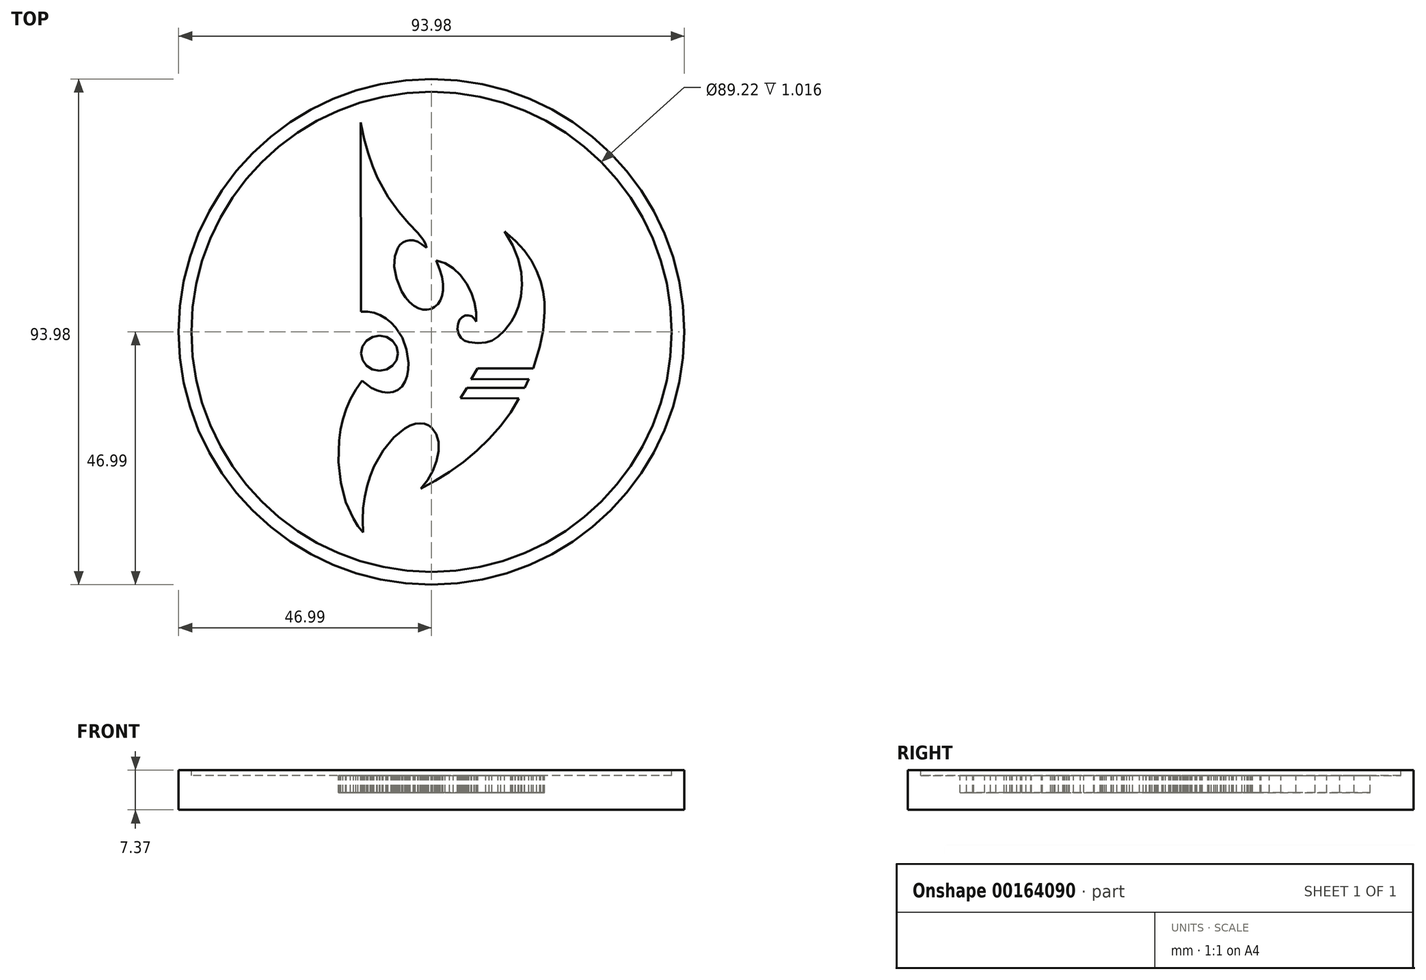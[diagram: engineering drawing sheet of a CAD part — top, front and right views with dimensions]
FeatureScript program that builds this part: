
annotation { "Feature Type Name" : "Feature", "Feature Type Description" : "" }
export const myFeature = defineFeature(function(context is Context, id is Id, definition is map)
    precondition{}
    {
        {
            var Q0;
            Q0=qCreatedBy(makeId("Front.planeOp"),FACE);
            var sketch = newSketch(context, id + "F0", { "sketchPlane" : qUnion([Q0])});
            skLineSegment(sketch, "E0", {"start": v(-47, 7.37) * mm, "end": v(-44.6, 7.37) * mm});
            skLineSegment(sketch, "E1", {"start": v(-44.6, 7.37) * mm, "end": v(-44.6, 6.35) * mm});
            skLineSegment(sketch, "E2", {"start": v(-44.6, 6.35) * mm, "end": v(0, 6.35) * mm});
            skLineSegment(sketch, "E3", {"start": v(0, 6.35) * mm, "end": v(0, 0) * mm});
            skLineSegment(sketch, "E4", {"start": v(0, 0) * mm, "end": v(-47, 0) * mm});
            skLineSegment(sketch, "E5", {"start": v(-47, 0) * mm, "end": v(-47, 7.37) * mm});
            skSolve(sketch);
        }
        {
            var Q0;
            Q0=makeQuery(id+"F0.imprint","IMPRINT",FACE,{"disambiguationData":[TD([[makeQuery(id+"F0.imprint","IMPRINT",EDGE,{"derivedFrom":sQuery(id+"F0.wireOp",EDGE,"E0")}),-1.0]])]});
            var Q1;
            Q1=sQuery(id+"F0.wireOp",EDGE,"E3");
            revolve(context, id + "F1", {"entities" : qUnion([Q0]), "axis" : qUnion([Q1]), "revolveType" : RevolveType.FULL});
        }
        {
            var Q0;
            Q0=makeQuery(id+"F1.opRevolve","SWEPT_FACE",FACE,{"disambiguationData":[OSD([sQuery(id+"F0.wireOp",EDGE,"E2")])]});
            var sketch = newSketch(context, id + "F2", { "sketchPlane" : qUnion([Q0])});
            skLineSegment(sketch, "E6", {"start": v(-13.1, 3.76) * mm, "end": v(-13.14, 38.91) * mm});
            skLineSegment(sketch, "E7", {"start": v(-13.14, 38.91) * mm, "end": v(-12.53, 35.9) * mm});
            skLineSegment(sketch, "E8", {"start": v(-12.53, 35.9) * mm, "end": v(-11.8, 33.21) * mm});
            skLineSegment(sketch, "E9", {"start": v(-11.8, 33.21) * mm, "end": v(-10.96, 30.8) * mm});
            skLineSegment(sketch, "E10", {"start": v(-10.96, 30.8) * mm, "end": v(-10.06, 28.67) * mm});
            skLineSegment(sketch, "E11", {"start": v(-10.06, 28.67) * mm, "end": v(-8.1, 25.1) * mm});
            skLineSegment(sketch, "E12", {"start": v(-8.1, 25.1) * mm, "end": v(-6.08, 22.32) * mm});
            skLineSegment(sketch, "E13", {"start": v(-6.08, 22.32) * mm, "end": v(-4.18, 20.16) * mm});
            skLineSegment(sketch, "E14", {"start": v(-4.18, 20.16) * mm, "end": v(-2.58, 18.44) * mm});
            skLineSegment(sketch, "E15", {"start": v(-2.58, 18.44) * mm, "end": v(-1.44, 16.97) * mm});
            skLineSegment(sketch, "E16", {"start": v(-1.44, 16.97) * mm, "end": v(-1.1, 16.29) * mm});
            skLineSegment(sketch, "E17", {"start": v(-1.1, 16.29) * mm, "end": v(-0.93, 15.6) * mm});
            skLineSegment(sketch, "E18", {"start": v(-0.93, 15.6) * mm, "end": v(-1.78, 16.28) * mm});
            skLineSegment(sketch, "E19", {"start": v(-1.78, 16.28) * mm, "end": v(-2.59, 16.74) * mm});
            skLineSegment(sketch, "E20", {"start": v(-2.59, 16.74) * mm, "end": v(-3.35, 16.99) * mm});
            skLineSegment(sketch, "E21", {"start": v(-3.35, 16.99) * mm, "end": v(-4.07, 17.04) * mm});
            skLineSegment(sketch, "E22", {"start": v(-4.07, 17.04) * mm, "end": v(-4.73, 16.92) * mm});
            skLineSegment(sketch, "E23", {"start": v(-4.73, 16.92) * mm, "end": v(-5.32, 16.62) * mm});
            skLineSegment(sketch, "E24", {"start": v(-5.32, 16.62) * mm, "end": v(-5.83, 16.18) * mm});
            skLineSegment(sketch, "E25", {"start": v(-5.83, 16.18) * mm, "end": v(-6.26, 15.6) * mm});
            skLineSegment(sketch, "E26", {"start": v(-6.26, 15.6) * mm, "end": v(-6.82, 14.05) * mm});
            skLineSegment(sketch, "E27", {"start": v(-6.82, 14.05) * mm, "end": v(-6.93, 12.12) * mm});
            skLineSegment(sketch, "E28", {"start": v(-6.93, 12.12) * mm, "end": v(-6.52, 9.9) * mm});
            skLineSegment(sketch, "E29", {"start": v(-6.52, 9.9) * mm, "end": v(-5.53, 7.5) * mm});
            skLineSegment(sketch, "E30", {"start": v(-5.53, 7.5) * mm, "end": v(-4.83, 6.4) * mm});
            skLineSegment(sketch, "E31", {"start": v(-4.83, 6.4) * mm, "end": v(-4.07, 5.5) * mm});
            skLineSegment(sketch, "E32", {"start": v(-4.07, 5.5) * mm, "end": v(-3.27, 4.85) * mm});
            skLineSegment(sketch, "E33", {"start": v(-3.27, 4.85) * mm, "end": v(-2.45, 4.4) * mm});
            skLineSegment(sketch, "E34", {"start": v(-2.45, 4.4) * mm, "end": v(-1.63, 4.16) * mm});
            skLineSegment(sketch, "E35", {"start": v(-1.63, 4.16) * mm, "end": v(-0.84, 4.12) * mm});
            skLineSegment(sketch, "E36", {"start": v(-0.84, 4.12) * mm, "end": v(-0.1, 4.27) * mm});
            skLineSegment(sketch, "E37", {"start": v(-0.1, 4.27) * mm, "end": v(0.58, 4.61) * mm});
            skLineSegment(sketch, "E38", {"start": v(0.58, 4.61) * mm, "end": v(1.16, 5.13) * mm});
            skLineSegment(sketch, "E39", {"start": v(1.16, 5.13) * mm, "end": v(1.63, 5.83) * mm});
            skLineSegment(sketch, "E40", {"start": v(1.63, 5.83) * mm, "end": v(1.97, 6.69) * mm});
            skLineSegment(sketch, "E41", {"start": v(1.97, 6.69) * mm, "end": v(2.15, 7.7) * mm});
            skLineSegment(sketch, "E42", {"start": v(2.15, 7.7) * mm, "end": v(2.14, 8.88) * mm});
            skLineSegment(sketch, "E43", {"start": v(2.14, 8.88) * mm, "end": v(1.94, 10.2) * mm});
            skLineSegment(sketch, "E44", {"start": v(1.94, 10.2) * mm, "end": v(1.52, 11.65) * mm});
            skLineSegment(sketch, "E45", {"start": v(1.52, 11.65) * mm, "end": v(0.85, 13.24) * mm});
            skLineSegment(sketch, "E46", {"start": v(0.85, 13.24) * mm, "end": v(2.52, 12.74) * mm});
            skLineSegment(sketch, "E47", {"start": v(2.52, 12.74) * mm, "end": v(4.04, 11.8) * mm});
            skLineSegment(sketch, "E48", {"start": v(4.04, 11.8) * mm, "end": v(5.37, 10.52) * mm});
            skLineSegment(sketch, "E49", {"start": v(5.37, 10.52) * mm, "end": v(6.5, 8.97) * mm});
            skLineSegment(sketch, "E50", {"start": v(6.5, 8.97) * mm, "end": v(7.39, 7.25) * mm});
            skLineSegment(sketch, "E51", {"start": v(7.39, 7.25) * mm, "end": v(8, 5.43) * mm});
            skLineSegment(sketch, "E52", {"start": v(8, 5.43) * mm, "end": v(8.32, 3.62) * mm});
            skLineSegment(sketch, "E53", {"start": v(8.32, 3.62) * mm, "end": v(8.3, 1.88) * mm});
            skLineSegment(sketch, "E54", {"start": v(8.3, 1.88) * mm, "end": v(7.95, 2.5) * mm});
            skLineSegment(sketch, "E55", {"start": v(7.95, 2.5) * mm, "end": v(7.44, 2.9) * mm});
            skLineSegment(sketch, "E56", {"start": v(7.44, 2.9) * mm, "end": v(6.85, 3.07) * mm});
            skLineSegment(sketch, "E57", {"start": v(6.85, 3.07) * mm, "end": v(6.24, 3.02) * mm});
            skLineSegment(sketch, "E58", {"start": v(6.24, 3.02) * mm, "end": v(5.67, 2.74) * mm});
            skLineSegment(sketch, "E59", {"start": v(5.67, 2.74) * mm, "end": v(5.2, 2.22) * mm});
            skLineSegment(sketch, "E60", {"start": v(5.2, 2.22) * mm, "end": v(4.9, 1.48) * mm});
            skLineSegment(sketch, "E61", {"start": v(4.9, 1.48) * mm, "end": v(4.83, 0.5) * mm});
            skLineSegment(sketch, "E62", {"start": v(4.83, 0.5) * mm, "end": v(5.04, -0.46) * mm});
            skLineSegment(sketch, "E63", {"start": v(5.04, -0.46) * mm, "end": v(5.5, -1.16) * mm});
            skLineSegment(sketch, "E64", {"start": v(5.5, -1.16) * mm, "end": v(6.16, -1.64) * mm});
            skLineSegment(sketch, "E65", {"start": v(6.16, -1.64) * mm, "end": v(6.94, -1.93) * mm});
            skLineSegment(sketch, "E66", {"start": v(6.94, -1.93) * mm, "end": v(8.64, -2.1) * mm});
            skLineSegment(sketch, "E67", {"start": v(8.64, -2.1) * mm, "end": v(10.09, -1.98) * mm});
            skLineSegment(sketch, "E68", {"start": v(10.09, -1.98) * mm, "end": v(11.24, -1.62) * mm});
            skLineSegment(sketch, "E69", {"start": v(11.24, -1.62) * mm, "end": v(12.38, -0.88) * mm});
            skLineSegment(sketch, "E70", {"start": v(12.38, -0.88) * mm, "end": v(13.56, 0.28) * mm});
            skLineSegment(sketch, "E71", {"start": v(13.56, 0.28) * mm, "end": v(14.82, 1.88) * mm});
            skLineSegment(sketch, "E72", {"start": v(14.82, 1.88) * mm, "end": v(15.56, 3.16) * mm});
            skLineSegment(sketch, "E73", {"start": v(15.56, 3.16) * mm, "end": v(16.19, 4.75) * mm});
            skLineSegment(sketch, "E74", {"start": v(16.19, 4.75) * mm, "end": v(16.63, 6.63) * mm});
            skLineSegment(sketch, "E75", {"start": v(16.63, 6.63) * mm, "end": v(16.8, 8.75) * mm});
            skLineSegment(sketch, "E76", {"start": v(16.8, 8.75) * mm, "end": v(16.66, 11.05) * mm});
            skLineSegment(sketch, "E77", {"start": v(16.66, 11.05) * mm, "end": v(16.12, 13.5) * mm});
            skLineSegment(sketch, "E78", {"start": v(16.12, 13.5) * mm, "end": v(15.1, 16.05) * mm});
            skLineSegment(sketch, "E79", {"start": v(15.1, 16.05) * mm, "end": v(13.56, 18.65) * mm});
            skLineSegment(sketch, "E80", {"start": v(13.56, 18.65) * mm, "end": v(15.6, 16.9) * mm});
            skLineSegment(sketch, "E81", {"start": v(15.6, 16.9) * mm, "end": v(17.27, 15.08) * mm});
            skLineSegment(sketch, "E82", {"start": v(17.27, 15.08) * mm, "end": v(18.58, 13.2) * mm});
            skLineSegment(sketch, "E83", {"start": v(18.58, 13.2) * mm, "end": v(19.57, 11.3) * mm});
            skLineSegment(sketch, "E84", {"start": v(19.57, 11.3) * mm, "end": v(20.28, 9.37) * mm});
            skLineSegment(sketch, "E85", {"start": v(20.28, 9.37) * mm, "end": v(20.73, 7.44) * mm});
            skLineSegment(sketch, "E86", {"start": v(20.73, 7.44) * mm, "end": v(20.97, 5.55) * mm});
            skLineSegment(sketch, "E87", {"start": v(20.97, 5.55) * mm, "end": v(21.03, 3.7) * mm});
            skLineSegment(sketch, "E88", {"start": v(21.03, 3.7) * mm, "end": v(20.72, 0.24) * mm});
            skLineSegment(sketch, "E89", {"start": v(20.72, 0.24) * mm, "end": v(20.08, -2.78) * mm});
            skLineSegment(sketch, "E90", {"start": v(20.08, -2.78) * mm, "end": v(18.88, -6.81) * mm});
            skLineSegment(sketch, "E91", {"start": v(18.88, -6.81) * mm, "end": v(8.55, -6.78) * mm});
            skLineSegment(sketch, "E92", {"start": v(8.55, -6.78) * mm, "end": v(7.34, -8.8) * mm});
            skLineSegment(sketch, "E93", {"start": v(7.34, -8.8) * mm, "end": v(18.1, -8.78) * mm});
            skLineSegment(sketch, "E94", {"start": v(18.1, -8.78) * mm, "end": v(17.34, -10.44) * mm});
            skLineSegment(sketch, "E95", {"start": v(17.34, -10.44) * mm, "end": v(6.62, -10.44) * mm});
            skLineSegment(sketch, "E96", {"start": v(6.62, -10.44) * mm, "end": v(5.4, -12.34) * mm});
            skLineSegment(sketch, "E97", {"start": v(5.4, -12.34) * mm, "end": v(16.25, -12.37) * mm});
            skLineSegment(sketch, "E98", {"start": v(16.25, -12.37) * mm, "end": v(14.7, -14.98) * mm});
            skLineSegment(sketch, "E99", {"start": v(14.7, -14.98) * mm, "end": v(12.84, -17.48) * mm});
            skLineSegment(sketch, "E100", {"start": v(12.84, -17.48) * mm, "end": v(10.73, -19.87) * mm});
            skLineSegment(sketch, "E101", {"start": v(10.73, -19.87) * mm, "end": v(8.4, -22.1) * mm});
            skLineSegment(sketch, "E102", {"start": v(8.4, -22.1) * mm, "end": v(5.93, -24.18) * mm});
            skLineSegment(sketch, "E103", {"start": v(5.93, -24.18) * mm, "end": v(3.34, -26.06) * mm});
            skLineSegment(sketch, "E104", {"start": v(3.34, -26.06) * mm, "end": v(0.7, -27.71) * mm});
            skLineSegment(sketch, "E105", {"start": v(0.7, -27.71) * mm, "end": v(-1.96, -29.13) * mm});
            skLineSegment(sketch, "E106", {"start": v(-1.96, -29.13) * mm, "end": v(-0.72, -27.58) * mm});
            skLineSegment(sketch, "E107", {"start": v(-0.72, -27.58) * mm, "end": v(0.27, -25.84) * mm});
            skLineSegment(sketch, "E108", {"start": v(0.27, -25.84) * mm, "end": v(0.96, -24) * mm});
            skLineSegment(sketch, "E109", {"start": v(0.96, -24) * mm, "end": v(1.31, -22.18) * mm});
            skLineSegment(sketch, "E110", {"start": v(1.31, -22.18) * mm, "end": v(1.3, -20.48) * mm});
            skLineSegment(sketch, "E111", {"start": v(1.3, -20.48) * mm, "end": v(0.9, -19) * mm});
            skLineSegment(sketch, "E112", {"start": v(0.9, -19) * mm, "end": v(0.05, -17.84) * mm});
            skLineSegment(sketch, "E113", {"start": v(0.05, -17.84) * mm, "end": v(-0.55, -17.41) * mm});
            skLineSegment(sketch, "E114", {"start": v(-0.55, -17.41) * mm, "end": v(-1.27, -17.11) * mm});
            skLineSegment(sketch, "E115", {"start": v(-1.27, -17.11) * mm, "end": v(-2.1, -17) * mm});
            skLineSegment(sketch, "E116", {"start": v(-2.1, -17) * mm, "end": v(-3, -17.1) * mm});
            skLineSegment(sketch, "E117", {"start": v(-3, -17.1) * mm, "end": v(-3.96, -17.43) * mm});
            skLineSegment(sketch, "E118", {"start": v(-3.96, -17.43) * mm, "end": v(-4.96, -17.96) * mm});
            skLineSegment(sketch, "E119", {"start": v(-4.96, -17.96) * mm, "end": v(-7, -19.62) * mm});
            skLineSegment(sketch, "E120", {"start": v(-7, -19.62) * mm, "end": v(-8.95, -22) * mm});
            skLineSegment(sketch, "E121", {"start": v(-8.95, -22) * mm, "end": v(-10.66, -25.04) * mm});
            skLineSegment(sketch, "E122", {"start": v(-10.66, -25.04) * mm, "end": v(-11.37, -26.78) * mm});
            skLineSegment(sketch, "E123", {"start": v(-11.37, -26.78) * mm, "end": v(-11.96, -28.65) * mm});
            skLineSegment(sketch, "E124", {"start": v(-11.96, -28.65) * mm, "end": v(-12.41, -30.65) * mm});
            skLineSegment(sketch, "E125", {"start": v(-12.41, -30.65) * mm, "end": v(-12.7, -32.76) * mm});
            skLineSegment(sketch, "E126", {"start": v(-12.7, -32.76) * mm, "end": v(-12.8, -34.98) * mm});
            skLineSegment(sketch, "E127", {"start": v(-12.8, -34.98) * mm, "end": v(-12.71, -37.29) * mm});
            skLineSegment(sketch, "E128", {"start": v(-12.71, -37.29) * mm, "end": v(-13.67, -36.1) * mm});
            skLineSegment(sketch, "E129", {"start": v(-13.67, -36.1) * mm, "end": v(-14.52, -34.76) * mm});
            skLineSegment(sketch, "E130", {"start": v(-14.52, -34.76) * mm, "end": v(-15.93, -31.62) * mm});
            skLineSegment(sketch, "E131", {"start": v(-15.93, -31.62) * mm, "end": v(-16.88, -28.03) * mm});
            skLineSegment(sketch, "E132", {"start": v(-16.88, -28.03) * mm, "end": v(-17.31, -24.16) * mm});
            skLineSegment(sketch, "E133", {"start": v(-17.31, -24.16) * mm, "end": v(-17.19, -20.17) * mm});
            skLineSegment(sketch, "E134", {"start": v(-17.19, -20.17) * mm, "end": v(-16.9, -18.18) * mm});
            skLineSegment(sketch, "E135", {"start": v(-16.9, -18.18) * mm, "end": v(-16.45, -16.22) * mm});
            skLineSegment(sketch, "E136", {"start": v(-16.45, -16.22) * mm, "end": v(-15.83, -14.32) * mm});
            skLineSegment(sketch, "E137", {"start": v(-15.83, -14.32) * mm, "end": v(-15.04, -12.48) * mm});
            skLineSegment(sketch, "E138", {"start": v(-15.04, -12.48) * mm, "end": v(-14.08, -10.74) * mm});
            skLineSegment(sketch, "E139", {"start": v(-14.08, -10.74) * mm, "end": v(-12.92, -9.1) * mm});
            skLineSegment(sketch, "E140", {"start": v(-12.92, -9.1) * mm, "end": v(-11.18, -10.42) * mm});
            skLineSegment(sketch, "E141", {"start": v(-11.18, -10.42) * mm, "end": v(-10.19, -10.89) * mm});
            skLineSegment(sketch, "E142", {"start": v(-10.19, -10.89) * mm, "end": v(-9.16, -11.18) * mm});
            skLineSegment(sketch, "E143", {"start": v(-9.16, -11.18) * mm, "end": v(-8.14, -11.29) * mm});
            skLineSegment(sketch, "E144", {"start": v(-8.14, -11.29) * mm, "end": v(-7.16, -11.17) * mm});
            skLineSegment(sketch, "E145", {"start": v(-7.16, -11.17) * mm, "end": v(-6.27, -10.8) * mm});
            skLineSegment(sketch, "E146", {"start": v(-6.27, -10.8) * mm, "end": v(-5.5, -10.14) * mm});
            skLineSegment(sketch, "E147", {"start": v(-5.5, -10.14) * mm, "end": v(-4.9, -9.24) * mm});
            skLineSegment(sketch, "E148", {"start": v(-4.9, -9.24) * mm, "end": v(-4.52, -8.18) * mm});
            skLineSegment(sketch, "E149", {"start": v(-4.52, -8.18) * mm, "end": v(-4.32, -7.01) * mm});
            skLineSegment(sketch, "E150", {"start": v(-4.32, -7.01) * mm, "end": v(-4.3, -5.78) * mm});
            skLineSegment(sketch, "E151", {"start": v(-4.3, -5.78) * mm, "end": v(-4.65, -3.29) * mm});
            skLineSegment(sketch, "E152", {"start": v(-4.65, -3.29) * mm, "end": v(-5.43, -1.08) * mm});
            skLineSegment(sketch, "E153", {"start": v(-5.43, -1.08) * mm, "end": v(-6.69, 0.84) * mm});
            skLineSegment(sketch, "E154", {"start": v(-6.69, 0.84) * mm, "end": v(-7.52, 1.7) * mm});
            skLineSegment(sketch, "E155", {"start": v(-7.52, 1.7) * mm, "end": v(-8.48, 2.47) * mm});
            skLineSegment(sketch, "E156", {"start": v(-8.48, 2.47) * mm, "end": v(-9.53, 3.1) * mm});
            skLineSegment(sketch, "E157", {"start": v(-9.53, 3.1) * mm, "end": v(-10.66, 3.54) * mm});
            skLineSegment(sketch, "E158", {"start": v(-10.66, 3.54) * mm, "end": v(-11.86, 3.77) * mm});
            skLineSegment(sketch, "E159", {"start": v(-11.86, 3.77) * mm, "end": v(-13.1, 3.76) * mm});
            skLineSegment(sketch, "E160", {"start": v(-6.25, -3.97) * mm, "end": v(-6.52, -5.26) * mm});
            skLineSegment(sketch, "E161", {"start": v(-6.52, -5.26) * mm, "end": v(-7.25, -6.3) * mm});
            skLineSegment(sketch, "E162", {"start": v(-7.25, -6.3) * mm, "end": v(-8.33, -7) * mm});
            skLineSegment(sketch, "E163", {"start": v(-8.33, -7) * mm, "end": v(-9.66, -7.27) * mm});
            skLineSegment(sketch, "E164", {"start": v(-9.66, -7.27) * mm, "end": v(-11, -7) * mm});
            skLineSegment(sketch, "E165", {"start": v(-11, -7) * mm, "end": v(-12.08, -6.3) * mm});
            skLineSegment(sketch, "E166", {"start": v(-12.08, -6.3) * mm, "end": v(-12.8, -5.26) * mm});
            skLineSegment(sketch, "E167", {"start": v(-12.8, -5.26) * mm, "end": v(-13.08, -3.97) * mm});
            skLineSegment(sketch, "E168", {"start": v(-13.08, -3.97) * mm, "end": v(-12.82, -2.71) * mm});
            skLineSegment(sketch, "E169", {"start": v(-12.82, -2.71) * mm, "end": v(-12.08, -1.65) * mm});
            skLineSegment(sketch, "E170", {"start": v(-12.08, -1.65) * mm, "end": v(-10.97, -0.93) * mm});
            skLineSegment(sketch, "E171", {"start": v(-10.97, -0.93) * mm, "end": v(-9.66, -0.68) * mm});
            skLineSegment(sketch, "E172", {"start": v(-9.66, -0.68) * mm, "end": v(-8.36, -0.93) * mm});
            skLineSegment(sketch, "E173", {"start": v(-8.36, -0.93) * mm, "end": v(-7.25, -1.65) * mm});
            skLineSegment(sketch, "E174", {"start": v(-7.25, -1.65) * mm, "end": v(-6.5, -2.71) * mm});
            skLineSegment(sketch, "E175", {"start": v(-6.5, -2.71) * mm, "end": v(-6.25, -3.97) * mm});
            skSolve(sketch);
        }
        {
            var Q0;
            Q0 = qSketchRegion(id + "F2", true);
            extrude(context, id + "F3", {"entities" : qUnion([Q0]), "operationType" : NewBodyOperationType.REMOVE, "oppositeDirection" : true, "depth" : 3.17 * mm});
        }
    });
